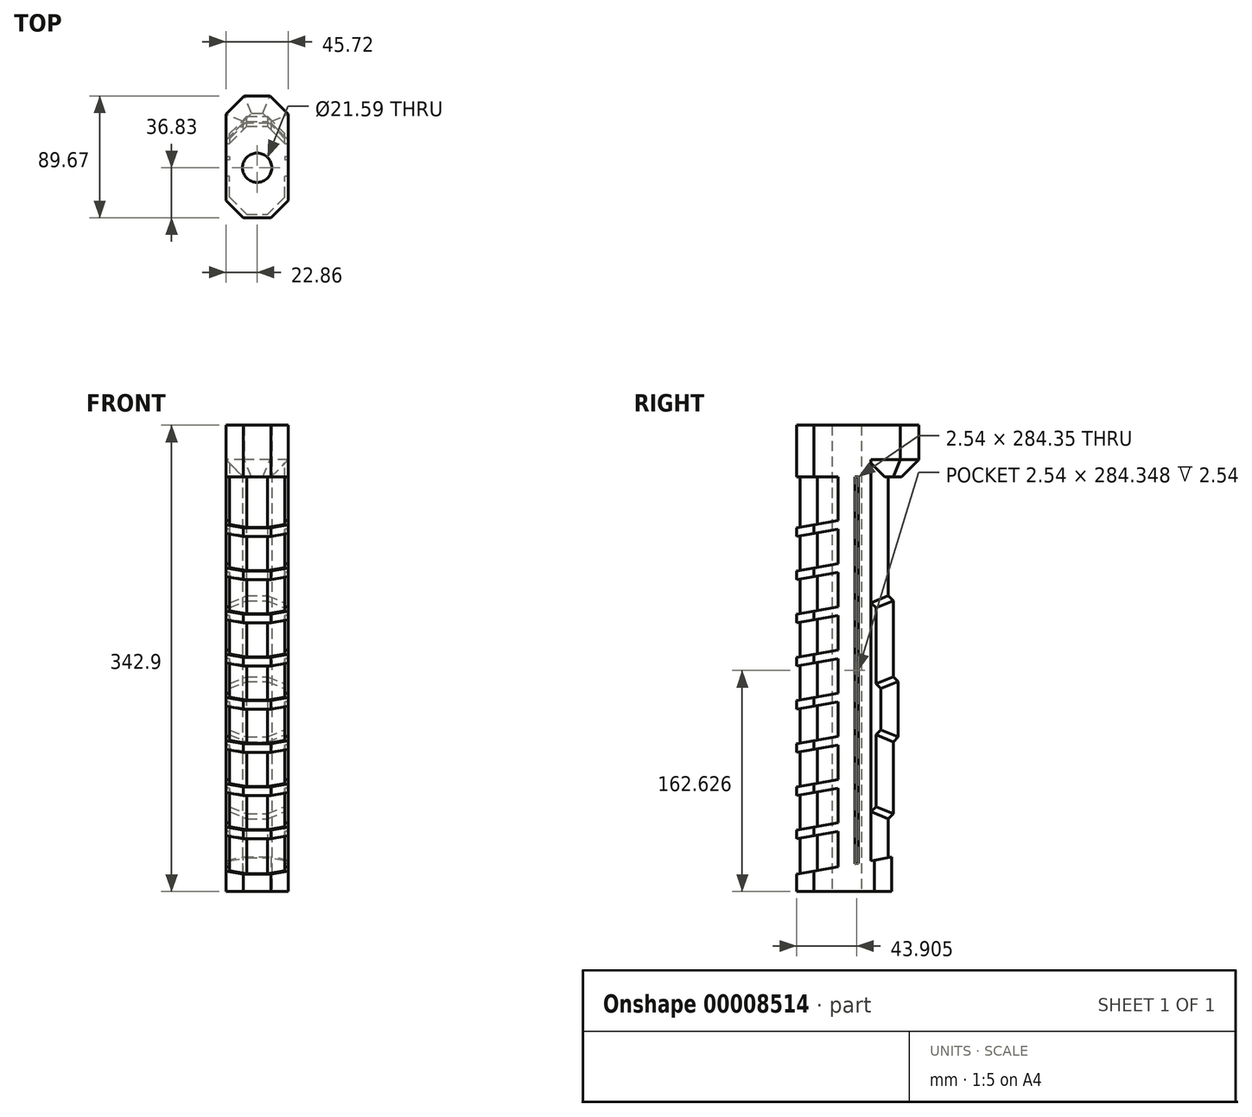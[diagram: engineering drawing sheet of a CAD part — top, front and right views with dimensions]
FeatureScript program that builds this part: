
annotation { "Feature Type Name" : "Feature", "Feature Type Description" : "" }
export const myFeature = defineFeature(function(context is Context, id is Id, definition is map)
    precondition{}
    {
        {
            var Q0;
            Q0=qCreatedBy(makeId("Top.planeOp"),FACE);
            var sketch = newSketch(context, id + "F0", { "sketchPlane" : qUnion([Q0])});
            skCircle(sketch, "E0", {"center": v(0, 0) * mm, "radius": 9.53 * mm});
            skSolve(sketch);
        }
        {
            var Q0;
            Q0 = qSketchRegion(id + "F0", true);
            extrude(context, id + "F1", {"entities" : qUnion([Q0]), "depth" : 38.1 * mm});
        }
        {
            var Q0;
            Q0=makeQuery(id+"F1.opExtrude","CAP_FACE",FACE,{"disambiguationData":[OSD([sQuery(id+"F0.wireOp",EDGE,"E0")])],"isStart":false});
            var sketch = newSketch(context, id + "F2", { "sketchPlane" : qUnion([Q0])});
            skLineSegment(sketch, "E1.bottom", {"start": v(-22.86, -17.78) * mm, "end": v(22.86, -17.78) * mm});
            skLineSegment(sketch, "E1.top", {"start": v(-22.86, 52.07) * mm, "end": v(22.86, 52.07) * mm});
            skLineSegment(sketch, "E1.left", {"start": v(-22.86, -17.78) * mm, "end": v(-22.86, 52.07) * mm});
            skLineSegment(sketch, "E1.right", {"start": v(22.86, -17.78) * mm, "end": v(22.86, 52.07) * mm});
            skSolve(sketch);
        }
        {
            var Q0;
            Q0=makeQuery(id+"F2.imprint","IMPRINT",FACE,{"disambiguationData":[TD([[makeQuery(id+"F2.imprint","IMPRINT",EDGE,{"derivedFrom":sQuery(id+"F2.wireOp",EDGE,"7003b8e0-f063-402b-a916-a828eb53b423.0")}),-1.0]])]});
            var Q1;
            {var subQ0=makeQuery(id+"F1.opExtrude","CAP_EDGE",EDGE,{"disambiguationData":[OSD([sQuery(id+"F0.wireOp",EDGE,"E0")])],"isStart":false});var subQ1=sQuery(id+"F2.wireOp",EDGE,"b5096f53-b7b5-46b7-9458-e08269a2e02d");var subQ3=makeQuery(id+"F2.imprint","INTERSECT",VERTEX,{"disambiguationData":[OD(0.0)],"derivedFrom":[subQ0,subQ1]});Q1=makeQuery(id+"F2.imprint","IMPRINT",FACE,{"disambiguationData":[TD([[makeQuery(id+"F2.imprint","IMPRINT",EDGE,{"disambiguationData":[TD([[subQ3,-1.0]])],"derivedFrom":subQ1}),-1.0]])]});}
            var Q2;
            {var subQ4=sQuery(id+"F2.wireOp",EDGE,"7003b8e0-f063-402b-a916-a828eb53b423.2");Q2=makeQuery(id+"F2.imprint","IMPRINT",FACE,{"disambiguationData":[TD([[makeQuery(id+"F2.imprint","IMPRINT",EDGE,{"derivedFrom":subQ4}),-1.0]])]});}
            var Q3;
            {var subQ0=makeQuery(id+"F1.opExtrude","CAP_EDGE",EDGE,{"disambiguationData":[OSD([sQuery(id+"F0.wireOp",EDGE,"E0")])],"isStart":false});var subQ1=sQuery(id+"F2.wireOp",EDGE,"b5096f53-b7b5-46b7-9458-e08269a2e02d");var subQ3=makeQuery(id+"F2.imprint","INTERSECT",VERTEX,{"disambiguationData":[OD(0.0)],"derivedFrom":[subQ0,subQ1]});Q3=makeQuery(id+"F2.imprint","IMPRINT",FACE,{"disambiguationData":[TD([[makeQuery(id+"F2.imprint","IMPRINT",EDGE,{"disambiguationData":[TD([[subQ3,-1.0]])],"derivedFrom":subQ1}),1.0]])]});}
            var Q4;
            Q4=makeQuery(id+"F2.imprint","IMPRINT",FACE,{"disambiguationData":[TD([[makeQuery(id+"F2.imprint","IMPRINT",EDGE,{"derivedFrom":makeQuery(id+"F1.opExtrude","CAP_EDGE",EDGE,{"disambiguationData":[OSD([sQuery(id+"F0.wireOp",EDGE,"E0")])],"isStart":false})}),1.0]])]});
            var Q5;
            Q5=makeQuery(id+"F2.imprint","IMPRINT",FACE,{"disambiguationData":[TD([[makeQuery(id+"F2.imprint","IMPRINT",EDGE,{"derivedFrom":sQuery(id+"F2.wireOp",EDGE,"E1.bottom")}),1.0]])]});
            extrude(context, id + "F3", {"entities" : qUnion([Q0, Q1, Q2, Q3, Q4, Q5]), "operationType" : NewBodyOperationType.ADD, "depth" : 25.4 * mm});
        }
        {
            var Q0;
            Q0=makeQuery(id+"F3.opExtrude","SWEPT_EDGE",EDGE,{"disambiguationData":[OSD([sQuery(id+"F2.wireOp",EDGE,"E1.bottom"),sQuery(id+"F2.wireOp",EDGE,"E1.left")])]});
            var Q1;
            Q1=makeQuery(id+"F3.opExtrude","SWEPT_EDGE",EDGE,{"disambiguationData":[OSD([sQuery(id+"F2.wireOp",EDGE,"E1.top"),sQuery(id+"F2.wireOp",EDGE,"E1.left")])]});
            var Q2;
            Q2=makeQuery(id+"F3.opExtrude","SWEPT_EDGE",EDGE,{"disambiguationData":[OSD([sQuery(id+"F2.wireOp",EDGE,"E1.bottom"),sQuery(id+"F2.wireOp",EDGE,"E1.right")])]});
            var Q3;
            Q3=makeQuery(id+"F3.opExtrude","SWEPT_EDGE",EDGE,{"disambiguationData":[OSD([sQuery(id+"F2.wireOp",EDGE,"E1.top"),sQuery(id+"F2.wireOp",EDGE,"E1.right")])]});
            chamfer(context, id + "F4", {"entities" : qUnion([Q0, Q1, Q2, Q3]), "width" : 12.7 * mm, "tangentPropagation" : true});
        }
        {
            var Q0;
            Q0=qCreatedBy(makeId("Right.planeOp"),FACE);
            var sketch = newSketch(context, id + "F5", { "sketchPlane" : qUnion([Q0])});
            skLineSegment(sketch, "E2.0", {"start": v(-5.08, 63.5) * mm, "end": v(39.37, 63.5) * mm});
            skLineSegment(sketch, "E3.0", {"start": v(-5.08, 63.5) * mm, "end": v(-17.78, 63.5) * mm});
            skLineSegment(sketch, "E3.1", {"start": v(-17.78, 63.5) * mm, "end": v(-17.78, 38.1) * mm});
            skLineSegment(sketch, "E4.0", {"start": v(52.07, 63.5) * mm, "end": v(39.37, 63.5) * mm});
            skLineSegment(sketch, "E5", {"start": v(-17.78, 50.8) * mm, "end": v(52.07, 63.5) * mm});
            skSolve(sketch);
        }
        {
            var Q0;
            Q0 = qSketchRegion(id + "F5", true);
            extrude(context, id + "F6", {"entities" : qUnion([Q0]), "operationType" : NewBodyOperationType.REMOVE, "oppositeDirection" : true, "depth" : 50.8 * mm, "symmetric" : true});
        }
        {
            var Q0;
            Q0=qCreatedBy(makeId("Right.planeOp"),FACE);
            var sketch = newSketch(context, id + "F7", { "sketchPlane" : qUnion([Q0])});
            skLineSegment(sketch, "E6.0", {"start": v(52.07, 38.1) * mm, "end": v(52.07, 63.5) * mm});
            skLineSegment(sketch, "E6.1", {"start": v(-17.78, 50.8) * mm, "end": v(-17.78, 38.1) * mm});
            skLineSegment(sketch, "E6.2", {"start": v(-5.08, 38.1) * mm, "end": v(39.37, 38.1) * mm});
            skLineSegment(sketch, "E6.3", {"start": v(-17.78, 38.1) * mm, "end": v(-5.08, 38.1) * mm});
            skLineSegment(sketch, "E6.4", {"start": v(39.37, 38.1) * mm, "end": v(52.07, 38.1) * mm});
            skLineSegment(sketch, "E7", {"start": v(-15.24, 38.1) * mm, "end": v(-15.24, 342.9) * mm});
            skLineSegment(sketch, "E8", {"start": v(49.53, 38.1) * mm, "end": v(49.53, 91.66) * mm});
            skPoint(sketch, "E9.orphan", {"position": v(49.53, 0) * mm});
            skLineSegment(sketch, "E10", {"start": v(-15.24, 342.9) * mm, "end": v(49.53, 342.9) * mm});
            skLineSegment(sketch, "E11", {"start": v(49.53, 91.66) * mm, "end": v(53.12, 95.25) * mm});
            skLineSegment(sketch, "E12", {"start": v(53.12, 95.25) * mm, "end": v(53.12, 148.19) * mm});
            skLineSegment(sketch, "E13", {"start": v(53.12, 148.19) * mm, "end": v(56.71, 151.78) * mm});
            skLineSegment(sketch, "E14", {"start": v(56.71, 151.78) * mm, "end": v(56.71, 192.57) * mm});
            skLineSegment(sketch, "E15", {"start": v(56.71, 192.57) * mm, "end": v(53.12, 196.16) * mm});
            skLineSegment(sketch, "E16", {"start": v(53.12, 196.16) * mm, "end": v(53.12, 252) * mm});
            skLineSegment(sketch, "E17", {"start": v(53.12, 252) * mm, "end": v(49.53, 255.6) * mm});
            skLineSegment(sketch, "E18.trimOffspring", {"start": v(49.53, 255.6) * mm, "end": v(49.53, 342.9) * mm});
            skSolve(sketch);
        }
        {
            var Q0;
            {var subQ3=sQuery(id+"F7.wireOp",EDGE,"E6.2");Q0=makeQuery(id+"F7.imprint","IMPRINT",FACE,{"disambiguationData":[TD([[makeQuery(id+"F7.imprint","IMPRINT",EDGE,{"derivedFrom":subQ3}),1.0]])]});}
            extrude(context, id + "F8", {"entities" : qUnion([Q0]), "operationType" : NewBodyOperationType.ADD, "oppositeDirection" : true, "depth" : 40.64 * mm, "symmetric" : true});
        }
        {
            var Q0;
            Q0=makeQuery(id+"F8.opExtrude","CAP_EDGE",EDGE,{"disambiguationData":[OSD([sQuery(id+"F7.wireOp",EDGE,"E8")])],"isStart":false});
            var Q1;
            Q1=makeQuery(id+"F8.opExtrude","CAP_EDGE",EDGE,{"disambiguationData":[OSD([sQuery(id+"F7.wireOp",EDGE,"E8")])],"isStart":true});
            var Q2;
            Q2=makeQuery(id+"F8.opExtrude","CAP_EDGE",EDGE,{"disambiguationData":[OSD([sQuery(id+"F7.wireOp",EDGE,"E7")])],"isStart":false});
            var Q3;
            Q3=makeQuery(id+"F8.opExtrude","CAP_EDGE",EDGE,{"disambiguationData":[OSD([sQuery(id+"F7.wireOp",EDGE,"E7")])],"isStart":true});
            var Q4;
            Q4=makeQuery(id+"F8.opExtrude","CAP_EDGE",EDGE,{"disambiguationData":[OSD([sQuery(id+"F7.wireOp",EDGE,"E18.trimOffspring")])],"isStart":false});
            var Q5;
            Q5=makeQuery(id+"F8.opExtrude","CAP_EDGE",EDGE,{"disambiguationData":[OSD([sQuery(id+"F7.wireOp",EDGE,"E18.trimOffspring")])],"isStart":true});
            var Q6;
            Q6=makeQuery(id+"F8.opExtrude","CAP_EDGE",EDGE,{"disambiguationData":[OSD([sQuery(id+"F7.wireOp",EDGE,"E12")])],"isStart":false});
            var Q7;
            Q7=makeQuery(id+"F8.opExtrude","CAP_EDGE",EDGE,{"disambiguationData":[OSD([sQuery(id+"F7.wireOp",EDGE,"E11")])],"isStart":false});
            var Q8;
            Q8=makeQuery(id+"F8.opExtrude","CAP_EDGE",EDGE,{"disambiguationData":[OSD([sQuery(id+"F7.wireOp",EDGE,"E14")])],"isStart":false});
            var Q9;
            Q9=makeQuery(id+"F8.opExtrude","CAP_EDGE",EDGE,{"disambiguationData":[OSD([sQuery(id+"F7.wireOp",EDGE,"E13")])],"isStart":false});
            var Q10;
            Q10=makeQuery(id+"F8.opExtrude","CAP_EDGE",EDGE,{"disambiguationData":[OSD([sQuery(id+"F7.wireOp",EDGE,"E15")])],"isStart":false});
            var Q11;
            Q11=makeQuery(id+"F8.opExtrude","CAP_EDGE",EDGE,{"disambiguationData":[OSD([sQuery(id+"F7.wireOp",EDGE,"E16")])],"isStart":false});
            var Q12;
            Q12=makeQuery(id+"F8.opExtrude","CAP_EDGE",EDGE,{"disambiguationData":[OSD([sQuery(id+"F7.wireOp",EDGE,"E17")])],"isStart":false});
            var Q13;
            Q13=makeQuery(id+"F8.opExtrude","CAP_EDGE",EDGE,{"disambiguationData":[OSD([sQuery(id+"F7.wireOp",EDGE,"E11")])],"isStart":true});
            var Q14;
            Q14=makeQuery(id+"F8.opExtrude","CAP_EDGE",EDGE,{"disambiguationData":[OSD([sQuery(id+"F7.wireOp",EDGE,"E12")])],"isStart":true});
            var Q15;
            Q15=makeQuery(id+"F8.opExtrude","CAP_EDGE",EDGE,{"disambiguationData":[OSD([sQuery(id+"F7.wireOp",EDGE,"E13")])],"isStart":true});
            var Q16;
            Q16=makeQuery(id+"F8.opExtrude","CAP_EDGE",EDGE,{"disambiguationData":[OSD([sQuery(id+"F7.wireOp",EDGE,"E14")])],"isStart":true});
            var Q17;
            Q17=makeQuery(id+"F8.opExtrude","CAP_EDGE",EDGE,{"disambiguationData":[OSD([sQuery(id+"F7.wireOp",EDGE,"E15")])],"isStart":true});
            var Q18;
            Q18=makeQuery(id+"F8.opExtrude","CAP_EDGE",EDGE,{"disambiguationData":[OSD([sQuery(id+"F7.wireOp",EDGE,"E16")])],"isStart":true});
            var Q19;
            Q19=makeQuery(id+"F8.opExtrude","CAP_EDGE",EDGE,{"disambiguationData":[OSD([sQuery(id+"F7.wireOp",EDGE,"E17")])],"isStart":true});
            chamfer(context, id + "F9", {"entities" : qUnion([Q0, Q1, Q2, Q3, Q4, Q5, Q6, Q7, Q8, Q9, Q10, Q11, Q12, Q13, Q14, Q15, Q16, Q17, Q18, Q19]), "width" : 12.7 * mm, "tangentPropagation" : true});
        }
        {
            var Q0;
            Q0=qCreatedBy(makeId("Right.planeOp"),FACE);
            var sketch = newSketch(context, id + "F10", { "sketchPlane" : qUnion([Q0])});
            skLineSegment(sketch, "E19.0", {"start": v(-5.08, 38.1) * mm, "end": v(39.37, 38.1) * mm});
            skLineSegment(sketch, "E19.1", {"start": v(-15.24, 38.1) * mm, "end": v(-5.08, 38.1) * mm});
            skLineSegment(sketch, "E19.2", {"start": v(41.91, 38.1) * mm, "end": v(52.07, 38.1) * mm});
            skLineSegment(sketch, "E19.3", {"start": v(-17.78, 50.8) * mm, "end": v(-17.78, 38.1) * mm});
            skLineSegment(sketch, "E20.0", {"start": v(36.83, 342.9) * mm, "end": v(36.83, 250.33) * mm});
            skLineSegment(sketch, "E21", {"start": v(12.7, 82.42) * mm, "end": v(-17.78, 76.87) * mm});
            skLineSegment(sketch, "E22", {"start": v(-17.78, 76.87) * mm, "end": v(-17.78, 83.21) * mm});
            skLineSegment(sketch, "E23", {"start": v(-17.78, 83.21) * mm, "end": v(12.7, 88.75) * mm});
            skLineSegment(sketch, "E24", {"start": v(12.7, 38.1) * mm, "end": v(12.7, 82.42) * mm});
            skLineSegment(sketch, "E25.trimOffspring", {"start": v(12.7, 88.75) * mm, "end": v(12.7, 114.17) * mm});
            skLineSegment(sketch, "E26.0.1.0", {"start": v(12.7, 114.17) * mm, "end": v(-17.78, 108.62) * mm});
            skLineSegment(sketch, "E26.0.1.1", {"start": v(-17.78, 114.96) * mm, "end": v(12.7, 120.5) * mm});
            skLineSegment(sketch, "E26.0.1.2", {"start": v(-17.78, 108.62) * mm, "end": v(-17.78, 114.96) * mm});
            skLineSegment(sketch, "E26.0.2.0", {"start": v(12.7, 145.92) * mm, "end": v(-17.78, 140.37) * mm});
            skLineSegment(sketch, "E26.0.2.1", {"start": v(-17.78, 146.71) * mm, "end": v(12.7, 152.25) * mm});
            skLineSegment(sketch, "E26.0.2.2", {"start": v(-17.78, 140.37) * mm, "end": v(-17.78, 146.71) * mm});
            skLineSegment(sketch, "E26.0.3.0", {"start": v(12.7, 177.67) * mm, "end": v(-17.78, 172.12) * mm});
            skLineSegment(sketch, "E26.0.3.1", {"start": v(-17.78, 178.46) * mm, "end": v(12.7, 184) * mm});
            skLineSegment(sketch, "E26.0.3.2", {"start": v(-17.78, 172.12) * mm, "end": v(-17.78, 178.46) * mm});
            skLineSegment(sketch, "E26.0.4.0", {"start": v(12.7, 209.42) * mm, "end": v(-17.78, 203.87) * mm});
            skLineSegment(sketch, "E26.0.4.1", {"start": v(-17.78, 210.21) * mm, "end": v(12.7, 215.75) * mm});
            skLineSegment(sketch, "E26.0.4.2", {"start": v(-17.78, 203.87) * mm, "end": v(-17.78, 210.21) * mm});
            skLineSegment(sketch, "E26.0.5.0", {"start": v(12.7, 241.17) * mm, "end": v(-17.78, 235.62) * mm});
            skLineSegment(sketch, "E26.0.5.1", {"start": v(-17.78, 241.96) * mm, "end": v(12.7, 247.5) * mm});
            skLineSegment(sketch, "E26.0.5.2", {"start": v(-17.78, 235.62) * mm, "end": v(-17.78, 241.96) * mm});
            skLineSegment(sketch, "E26.0.6.0", {"start": v(12.7, 272.92) * mm, "end": v(-17.78, 267.37) * mm});
            skLineSegment(sketch, "E26.0.6.1", {"start": v(-17.78, 273.71) * mm, "end": v(12.7, 279.25) * mm});
            skLineSegment(sketch, "E26.0.6.2", {"start": v(-17.78, 267.37) * mm, "end": v(-17.78, 273.71) * mm});
            skLineSegment(sketch, "E26.0.7.0", {"start": v(12.7, 304.67) * mm, "end": v(-17.78, 299.12) * mm});
            skLineSegment(sketch, "E26.0.7.1", {"start": v(-17.78, 305.46) * mm, "end": v(12.7, 311) * mm});
            skLineSegment(sketch, "E26.0.7.2", {"start": v(-17.78, 299.12) * mm, "end": v(-17.78, 305.46) * mm});
            skLineSegment(sketch, "E26.0.7.3", {"start": v(36.83, 260.35) * mm, "end": v(36.83, 342.9) * mm});
            skLineSegment(sketch, "E26.direction1", {"start": v(-17.78, 76.87) * mm, "end": v(7.62, 76.87) * mm, "construction": true});
            skLineSegment(sketch, "E26.direction2", {"start": v(-17.78, 76.87) * mm, "end": v(-17.78, 108.62) * mm, "construction": true});
            skLineSegment(sketch, "E27.trimOffspring", {"start": v(12.7, 120.5) * mm, "end": v(12.7, 145.92) * mm});
            skLineSegment(sketch, "E28.trimOffspring", {"start": v(12.7, 152.25) * mm, "end": v(12.7, 177.67) * mm});
            skLineSegment(sketch, "E29.trimOffspring", {"start": v(12.7, 184) * mm, "end": v(12.7, 209.42) * mm});
            skLineSegment(sketch, "E30.trimOffspring", {"start": v(12.7, 215.75) * mm, "end": v(12.7, 241.17) * mm});
            skLineSegment(sketch, "E31.trimOffspring", {"start": v(12.7, 247.5) * mm, "end": v(12.7, 272.92) * mm});
            skLineSegment(sketch, "E32.trimOffspring", {"start": v(12.7, 279.25) * mm, "end": v(12.7, 304.67) * mm});
            skLineSegment(sketch, "E33.trimOffspring", {"start": v(12.7, 311) * mm, "end": v(12.7, 342.9) * mm});
            skLineSegment(sketch, "E34", {"start": v(36.83, 342.9) * mm, "end": v(12.7, 342.9) * mm});
            skLineSegment(sketch, "E35", {"start": v(36.83, 342.9) * mm, "end": v(36.83, 38.1) * mm});
            skLineSegment(sketch, "E36", {"start": v(24.85, 38.1) * mm, "end": v(24.85, 350.34) * mm});
            skLineSegment(sketch, "E37", {"start": v(24.85, 350.34) * mm, "end": v(27.4, 350.34) * mm});
            skLineSegment(sketch, "E38", {"start": v(27.4, 350.34) * mm, "end": v(27.4, 38.1) * mm});
            skSolve(sketch);
        }
        {
            var Q0;
            Q0=makeQuery(id+"F10.imprint","IMPRINT",FACE,{"disambiguationData":[TD([[makeQuery(id+"F10.imprint","IMPRINT",EDGE,{"derivedFrom":sQuery(id+"F10.wireOp",EDGE,"E21")}),-1.0]])]});
            var Q1;
            {var subQ3=sQuery(id+"F10.wireOp",EDGE,"E19.0");var subQ5=sQuery(id+"F10.wireOp",EDGE,"E35");var subQ6=makeQuery(id+"F10.imprint","INTERSECT",VERTEX,{"derivedFrom":[subQ3,subQ5]});Q1=makeQuery(id+"F10.imprint","IMPRINT",FACE,{"disambiguationData":[TD([[makeQuery(id+"F10.imprint","IMPRINT",EDGE,{"disambiguationData":[TD([[subQ6,1.0]])],"derivedFrom":subQ3}),1.0]])]});}
            extrude(context, id + "F11", {"entities" : qUnion([Q0, Q1]), "operationType" : NewBodyOperationType.ADD, "depth" : 45.72 * mm, "symmetric" : true});
        }
        {
            var Q0;
            Q0=makeQuery(id+"F11.opExtrude","CAP_EDGE",EDGE,{"disambiguationData":[OSD([sQuery(id+"F10.wireOp",EDGE,"E26.0.7.2")])],"isStart":true});
            var Q1;
            Q1=makeQuery(id+"F11.opExtrude","CAP_EDGE",EDGE,{"disambiguationData":[OSD([sQuery(id+"F10.wireOp",EDGE,"E26.0.6.2")])],"isStart":true});
            var Q2;
            Q2=makeQuery(id+"F11.opExtrude","CAP_EDGE",EDGE,{"disambiguationData":[OSD([sQuery(id+"F10.wireOp",EDGE,"E26.0.5.2")])],"isStart":true});
            var Q3;
            Q3=makeQuery(id+"F11.opExtrude","CAP_EDGE",EDGE,{"disambiguationData":[OSD([sQuery(id+"F10.wireOp",EDGE,"E26.0.4.2")])],"isStart":true});
            var Q4;
            Q4=makeQuery(id+"F11.opExtrude","CAP_EDGE",EDGE,{"disambiguationData":[OSD([sQuery(id+"F10.wireOp",EDGE,"E26.0.3.2")])],"isStart":true});
            var Q5;
            Q5=makeQuery(id+"F11.opExtrude","CAP_EDGE",EDGE,{"disambiguationData":[OSD([sQuery(id+"F10.wireOp",EDGE,"E26.0.2.2")])],"isStart":true});
            var Q6;
            Q6=makeQuery(id+"F11.opExtrude","CAP_EDGE",EDGE,{"disambiguationData":[OSD([sQuery(id+"F10.wireOp",EDGE,"E26.0.1.2")])],"isStart":true});
            var Q7;
            Q7=makeQuery(id+"F11.opExtrude","CAP_EDGE",EDGE,{"disambiguationData":[OSD([sQuery(id+"F10.wireOp",EDGE,"E22")])],"isStart":true});
            var Q8;
            Q8=makeQuery(id+"F11.opExtrude","CAP_EDGE",EDGE,{"disambiguationData":[OSD([sQuery(id+"F10.wireOp",EDGE,"E22")])],"isStart":false});
            var Q9;
            Q9=makeQuery(id+"F11.opExtrude","CAP_EDGE",EDGE,{"disambiguationData":[OSD([sQuery(id+"F10.wireOp",EDGE,"E26.0.1.2")])],"isStart":false});
            var Q10;
            Q10=makeQuery(id+"F11.opExtrude","CAP_EDGE",EDGE,{"disambiguationData":[OSD([sQuery(id+"F10.wireOp",EDGE,"E26.0.2.2")])],"isStart":false});
            var Q11;
            Q11=makeQuery(id+"F11.opExtrude","CAP_EDGE",EDGE,{"disambiguationData":[OSD([sQuery(id+"F10.wireOp",EDGE,"E26.0.3.2")])],"isStart":false});
            var Q12;
            Q12=makeQuery(id+"F11.opExtrude","CAP_EDGE",EDGE,{"disambiguationData":[OSD([sQuery(id+"F10.wireOp",EDGE,"E26.0.4.2")])],"isStart":false});
            var Q13;
            Q13=makeQuery(id+"F11.opExtrude","CAP_EDGE",EDGE,{"disambiguationData":[OSD([sQuery(id+"F10.wireOp",EDGE,"E26.0.5.2")])],"isStart":false});
            var Q14;
            Q14=makeQuery(id+"F11.opExtrude","CAP_EDGE",EDGE,{"disambiguationData":[OSD([sQuery(id+"F10.wireOp",EDGE,"E26.0.6.2")])],"isStart":false});
            var Q15;
            Q15=makeQuery(id+"F11.opExtrude","CAP_EDGE",EDGE,{"disambiguationData":[OSD([sQuery(id+"F10.wireOp",EDGE,"E26.0.7.2")])],"isStart":false});
            chamfer(context, id + "F12", {"entities" : qUnion([Q0, Q1, Q2, Q3, Q4, Q5, Q6, Q7, Q8, Q9, Q10, Q11, Q12, Q13, Q14, Q15]), "width" : 12.7 * mm, "tangentPropagation" : true});
        }
        {
            var Q0;
            {var subQ0=sQuery(id+"F10.wireOp",EDGE,"E34");Q0=makeQuery(id+"F11.boolean.opBoolean","MERGE",FACE,{"derivedFrom":[makeQuery(id+"F8.opExtrude","SWEPT_FACE",FACE,{"disambiguationData":[OSD([sQuery(id+"F7.wireOp",EDGE,"E10")])]}),makeQuery(id+"F11.opExtrude","SWEPT_FACE",FACE,{"disambiguationData":[OSD([subQ0]),TDD([makeQuery(id+"F10.imprint","IMPRINT",EDGE,{"disambiguationData":[TD([[makeQuery(id+"F10.imprint","INTERSECT",VERTEX,{"derivedFrom":[subQ0,sQuery(id+"F10.wireOp",EDGE,"E35")]}),-1.0]])],"derivedFrom":subQ0})])]}),makeQuery(id+"F11.opExtrude","SWEPT_FACE",FACE,{"disambiguationData":[OSD([subQ0]),TDD([makeQuery(id+"F10.imprint","IMPRINT",EDGE,{"disambiguationData":[TD([[makeQuery(id+"F10.imprint","INTERSECT",VERTEX,{"derivedFrom":[sQuery(id+"F10.wireOp",EDGE,"E33.trimOffspring"),subQ0]}),1.0]])],"derivedFrom":subQ0})])]})]});}
            var sketch = newSketch(context, id + "F13", { "sketchPlane" : qUnion([Q0])});
            skLineSegment(sketch, "E39.0", {"start": v(-22.86, -5.08) * mm, "end": v(-22.86, 39.37) * mm});
            skLineSegment(sketch, "E39.1", {"start": v(-20.32, 41.91) * mm, "end": v(-10.16, 52.07) * mm});
            skLineSegment(sketch, "E40.0", {"start": v(-12.7, -15.24) * mm, "end": v(-22.86, -5.08) * mm});
            skLineSegment(sketch, "E40.1", {"start": v(-10.16, -17.78) * mm, "end": v(10.16, -17.78) * mm});
            skLineSegment(sketch, "E40.2", {"start": v(20.32, -7.62) * mm, "end": v(10.16, -17.78) * mm});
            skLineSegment(sketch, "E41.0", {"start": v(22.86, -5.08) * mm, "end": v(22.86, 39.37) * mm});
            skLineSegment(sketch, "E41.1", {"start": v(12.7, 49.53) * mm, "end": v(22.86, 39.37) * mm});
            skLineSegment(sketch, "E42", {"start": v(-22.86, -5.08) * mm, "end": v(-22.86, 58.42) * mm});
            skLineSegment(sketch, "E43", {"start": v(-22.86, 58.42) * mm, "end": v(-9.39, 71.9) * mm});
            skLineSegment(sketch, "E44", {"start": v(-9.39, 71.9) * mm, "end": v(9.39, 71.9) * mm});
            skLineSegment(sketch, "E45", {"start": v(9.39, 71.9) * mm, "end": v(22.86, 58.42) * mm});
            skLineSegment(sketch, "E46", {"start": v(22.86, -5.08) * mm, "end": v(22.86, 58.42) * mm});
            skLineSegment(sketch, "E47", {"start": v(-22.86, -5.08) * mm, "end": v(-10.16, -17.78) * mm});
            skLineSegment(sketch, "E48", {"start": v(10.16, -17.78) * mm, "end": v(22.86, -5.08) * mm});
            skPoint(sketch, "E39.2.end.orphan", {"position": v(10.16, 52.07) * mm});
            skSolve(sketch);
        }
        {
            var Q0;
            {var subQ52=sQuery(id+"F13.wireOp",EDGE,"E43");Q0=makeQuery(id+"F13.imprint","IMPRINT",FACE,{"disambiguationData":[TD([[makeQuery(id+"F13.imprint","IMPRINT",EDGE,{"derivedFrom":subQ52}),-1.0]])]});}
            var Q1;
            {var subQ46=sQuery(id+"F7.wireOp",EDGE,"E10");var subQ55=sQuery(id+"F7.wireOp",EDGE,"E7");Q1=makeQuery(id+"F13.imprint","IMPRINT",FACE,{"disambiguationData":[TD([[makeQuery(id+"F13.imprint","IMPRINT",EDGE,{"derivedFrom":makeQuery(id+"F8.opExtrude","SWEPT_EDGE",EDGE,{"disambiguationData":[OSD([subQ55,subQ46])]})}),1.0]])]});}
            var Q2;
            {var subQ63=sQuery(id+"F13.wireOp",EDGE,"E40.1");Q2=makeQuery(id+"F13.imprint","IMPRINT",FACE,{"disambiguationData":[TD([[makeQuery(id+"F13.imprint","IMPRINT",EDGE,{"derivedFrom":subQ63}),1.0]])]});}
            var Q3;
            {var subQ1=sQuery(id+"F10.wireOp",EDGE,"E36");var subQ2=makeQuery(id+"F11.opExtrude","SWEPT_FACE",FACE,{"disambiguationData":[OSD([subQ1])]});var subQ11=sQuery(id+"F7.wireOp",EDGE,"E10");Q3=makeQuery(id+"F13.imprint","IMPRINT",FACE,{"disambiguationData":[TD([[makeQuery(id+"F13.imprint","IMPRINT",EDGE,{"derivedFrom":makeQuery(id+"F11.boolean.opBoolean","SPLIT",EDGE,{"disambiguationData":[TD([subQ2])],"derivedFrom":makeQuery(id+"F8.opExtrude","CAP_EDGE",EDGE,{"disambiguationData":[OSD([subQ11])],"isStart":false})})}),1.0]])]});}
            var Q4;
            {var subQ1=sQuery(id+"F10.wireOp",EDGE,"E36");var subQ2=makeQuery(id+"F11.opExtrude","SWEPT_FACE",FACE,{"disambiguationData":[OSD([subQ1])]});var subQ11=sQuery(id+"F7.wireOp",EDGE,"E10");Q4=makeQuery(id+"F13.imprint","IMPRINT",FACE,{"disambiguationData":[TD([[makeQuery(id+"F13.imprint","IMPRINT",EDGE,{"derivedFrom":makeQuery(id+"F11.boolean.opBoolean","SPLIT",EDGE,{"disambiguationData":[TD([subQ2])],"derivedFrom":makeQuery(id+"F8.opExtrude","CAP_EDGE",EDGE,{"disambiguationData":[OSD([subQ11])],"isStart":true})})}),-1.0]])]});}
            extrude(context, id + "F14", {"entities" : qUnion([Q0, Q1, Q2, Q3, Q4]), "operationType" : NewBodyOperationType.ADD, "depth" : 38.1 * mm});
        }
        {
            var Q0;
            Q0=makeQuery(id+"F14.opExtrude","CAP_EDGE",EDGE,{"disambiguationData":[OSD([sQuery(id+"F13.wireOp",EDGE,"E44")])],"isStart":true});
            var Q1;
            {var subQ0=sQuery(id+"F13.wireOp",EDGE,"E46");var subQ2=sQuery(id+"F10.wireOp",EDGE,"E35");Q1=makeQuery(id+"F14.boolean.opBoolean","SPLIT",EDGE,{"disambiguationData":[TD([makeQuery(id+"F11.opExtrude","SWEPT_FACE",FACE,{"disambiguationData":[OSD([subQ2])]})])],"derivedFrom":makeQuery(id+"F14.opExtrude","CAP_EDGE",EDGE,{"disambiguationData":[OSD([subQ0])],"isStart":true})});}
            var Q2;
            {var subQ0=sQuery(id+"F13.wireOp",EDGE,"E42");var subQ2=sQuery(id+"F10.wireOp",EDGE,"E35");Q2=makeQuery(id+"F14.boolean.opBoolean","SPLIT",EDGE,{"disambiguationData":[TD([makeQuery(id+"F11.opExtrude","SWEPT_FACE",FACE,{"disambiguationData":[OSD([subQ2])]})])],"derivedFrom":makeQuery(id+"F14.opExtrude","CAP_EDGE",EDGE,{"disambiguationData":[OSD([subQ0])],"isStart":true})});}
            var Q3;
            Q3=makeQuery(id+"F14.opExtrude","CAP_EDGE",EDGE,{"disambiguationData":[OSD([sQuery(id+"F13.wireOp",EDGE,"E43")])],"isStart":true});
            var Q4;
            Q4=makeQuery(id+"F14.opExtrude","CAP_EDGE",EDGE,{"disambiguationData":[OSD([sQuery(id+"F13.wireOp",EDGE,"E45")])],"isStart":true});
            chamfer(context, id + "F15", {"entities" : qUnion([Q0, Q1, Q2, Q3, Q4]), "width" : 12.7 * mm, "tangentPropagation" : true});
        }
        {
            var Q0;
            Q0=makeQuery(id+"F14.opExtrude","CAP_FACE",FACE,{"disambiguationData":[OSD([sQuery(id+"F13.wireOp",EDGE,"E42"),sQuery(id+"F13.wireOp",EDGE,"E43"),sQuery(id+"F13.wireOp",EDGE,"E44"),sQuery(id+"F13.wireOp",EDGE,"E45"),sQuery(id+"F13.wireOp",EDGE,"E46"),sQuery(id+"F13.wireOp",EDGE,"E47"),sQuery(id+"F13.wireOp",EDGE,"E48"),sQuery(id+"F13.wireOp",EDGE,"E40.1")])],"isStart":false});
            var sketch = newSketch(context, id + "F16", { "sketchPlane" : qUnion([Q0])});
            skCircle(sketch, "E49", {"center": v(0, 31.75) * mm, "radius": 10.16 * mm});
            skSolve(sketch);
        }
        {
            var Q0;
            Q0=makeQuery(id+"F16.imprint","IMPRINT",FACE,{"disambiguationData":[TD([[makeQuery(id+"F16.imprint","IMPRINT",EDGE,{"derivedFrom":sQuery(id+"F16.wireOp",EDGE,"E49")}),1.0]])]});
            extrude(context, id + "F17", {"entities" : qUnion([Q0]), "operationType" : NewBodyOperationType.REMOVE, "oppositeDirection" : true, "depth" : 38.1 * mm});
        }
        {
            var Q0;
            Q0=makeQuery(id+"F1.opExtrude","CAP_FACE",FACE,{"disambiguationData":[OSD([sQuery(id+"F0.wireOp",EDGE,"E0")])],"isStart":true});
            extrude(context, id + "F18", {"entities" : qUnion([Q0]), "operationType" : NewBodyOperationType.REMOVE, "oppositeDirection" : true, "depth" : 38.1 * mm});
        }
        {
            var Q0;
            Q0=makeQuery(id+"F17.boolean.opBoolean","COPY",FACE,{"derivedFrom":makeQuery(id+"F17.opExtrude","CAP_FACE",FACE,{"disambiguationData":[OSD([sQuery(id+"F16.wireOp",EDGE,"E49")])],"isStart":false})});
            extrude(context, id + "F19", {"entities" : qUnion([Q0]), "operationType" : NewBodyOperationType.ADD, "depth" : 38.1 * mm});
        }
        {
            var Q0;
            Q0=makeQuery(id+"F18.boolean.opBoolean","MERGE",FACE,{"derivedFrom":[makeQuery(id+"F8.boolean.opBoolean","MERGE",FACE,{"derivedFrom":[makeQuery(id+"F3.opExtrude","CAP_FACE",FACE,{"disambiguationData":[OSD([sQuery(id+"F2.wireOp",EDGE,"E1.bottom"),sQuery(id+"F2.wireOp",EDGE,"E1.top"),sQuery(id+"F2.wireOp",EDGE,"E1.left"),sQuery(id+"F2.wireOp",EDGE,"E1.right")])],"isStart":true}),makeQuery(id+"F8.opExtrude","SWEPT_FACE",FACE,{"disambiguationData":[OSD([sQuery(id+"F7.wireOp",EDGE,"E6.2"),sQuery(id+"F7.wireOp",EDGE,"E6.3"),sQuery(id+"F7.wireOp",EDGE,"E6.4")])]})]}),makeQuery(id+"F18.opExtrude","CAP_FACE",FACE,{"disambiguationData":[OSD([sQuery(id+"F0.wireOp",EDGE,"E0")])],"isStart":false})]});
            var sketch = newSketch(context, id + "F20", { "sketchPlane" : qUnion([Q0])});
            skCircle(sketch, "E50", {"center": v(0, -19.05) * mm, "radius": 10.8 * mm});
            skSolve(sketch);
        }
        {
            var Q0;
            Q0=makeQuery(id+"F20.imprint","IMPRINT",FACE,{"disambiguationData":[TD([[makeQuery(id+"F20.imprint","IMPRINT",EDGE,{"derivedFrom":sQuery(id+"F20.wireOp",EDGE,"E50")}),1.0]])]});
            extrude(context, id + "F21", {"entities" : qUnion([Q0]), "operationType" : NewBodyOperationType.REMOVE, "oppositeDirection" : true, "depth" : 508 * mm});
        }
    });
